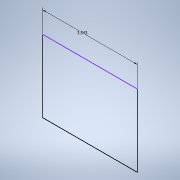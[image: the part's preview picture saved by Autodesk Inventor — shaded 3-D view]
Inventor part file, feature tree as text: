
AUTODESK INVENTOR PART (.ipt)
format: ipt  version: 2022 (Build 260153000, 153)  size: 85,504 bytes
history: native  units: in
note: dims shown in document units (in); Inventor stores cm internally (conversion verified against a paired STEP export)
features: sketch x1
ambient origin geometry x8: Origin, YZ Plane, XZ Plane, XY Plane, X Axis, Y Axis, Z Axis, Center Point
feature tree (1):
  sketch  "Sketch1"  dims[d0=3.5433in]
